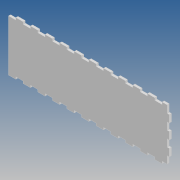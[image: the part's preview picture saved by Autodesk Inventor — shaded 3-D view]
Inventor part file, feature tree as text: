
AUTODESK INVENTOR PART (.ipt)
format: ipt  version: 2020 (Build 240168000, 168)  size: 192,512 bytes
history: native  units: mm
features: extrude x4, sketch x4, pattern_linear x3, other x1
ambient origin geometry x8: Origin, YZ Plane, XZ Plane, XY Plane, X Axis, Y Axis, Z Axis, Center Point
bodies: Body1 (feature_tree)
feature tree (12):
  other  "Твердое тело1"
  extrude  "Выдавливание1"  Depth=10.0mm
  pattern_linear  "Прямоуг.массив1"  Spacing1=3.0mm  [1 undecoded]
  extrude  "Выдавливание2"  Depth=3.0mm TaperAngle=0.0deg
  extrude  "Выдавливание3"  Depth=110.0mm
  pattern_linear  "Прямоуг.массив2"  Count1=7  [1 undecoded]
  extrude  "Выдавливание4"  Depth=3.0mm TaperAngle=0.0deg
  pattern_linear  "Прямоуг.массив3"  Spacing1=10.0mm  [1 undecoded]
  sketch  "Эскиз1"
  sketch  "Эскиз2"
  sketch  "Эскиз3"
  sketch  "Эскиз4"
note: 3 required parameter values undecoded (feature->parameter linkage not recoverable at this tier; creation-order binding heuristic only, values carry confidence <= 0.55)
